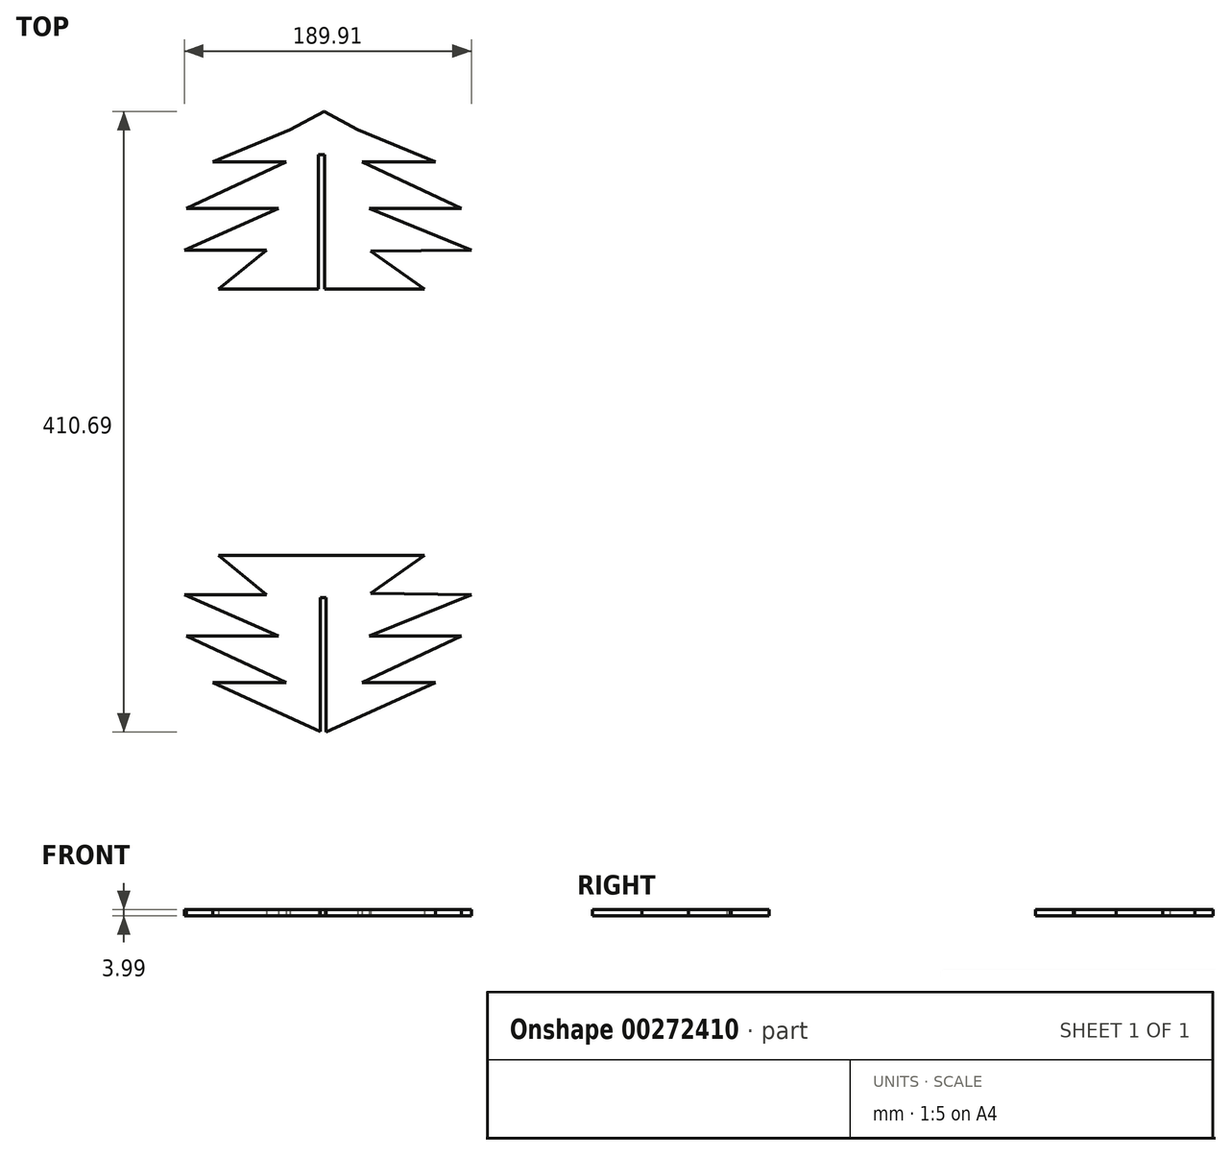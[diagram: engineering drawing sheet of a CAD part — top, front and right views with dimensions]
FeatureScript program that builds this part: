
annotation { "Feature Type Name" : "Feature", "Feature Type Description" : "" }
export const myFeature = defineFeature(function(context is Context, id is Id, definition is map)
    precondition{}
    {
        {
            var Q0;
            Q0=qCreatedBy(makeId("Top.planeOp"),FACE);
            var sketch = newSketch(context, id + "F0", { "sketchPlane" : qUnion([Q0])});
            skLineSegment(sketch, "E0.MirrorCS", {"start": v(-247.1, 88.4) * mm, "end": v(-298.41, 109.7) * mm});
            skLineSegment(sketch, "E1.MirrorCS", {"start": v(-295.66, 88.4) * mm, "end": v(-247.1, 88.4) * mm});
            skLineSegment(sketch, "E2.MirrorCS", {"start": v(-229.72, 57.49) * mm, "end": v(-295.66, 88.4) * mm});
            skLineSegment(sketch, "E3.MirrorCS", {"start": v(-290.86, 57.49) * mm, "end": v(-229.72, 57.49) * mm});
            skLineSegment(sketch, "E4.MirrorCS", {"start": v(-223.27, 30) * mm, "end": v(-290.86, 57.49) * mm});
            skLineSegment(sketch, "E5.MirrorCS", {"start": v(-289.8, 29.3) * mm, "end": v(-223.27, 30) * mm});
            skLineSegment(sketch, "E6.MirrorCS", {"start": v(-254.41, 4.11) * mm, "end": v(-289.8, 29.3) * mm});
            skLineSegment(sketch, "E7.MirrorCS", {"start": v(-320.45, 4.11) * mm, "end": v(-254.41, 4.11) * mm});
            skLineSegment(sketch, "E8.MirrorCS", {"start": v(-390.48, 4.11) * mm, "end": v(-324.44, 4.11) * mm});
            skLineSegment(sketch, "E9.MirrorCS", {"start": v(-390.48, 4.11) * mm, "end": v(-358.92, 30) * mm});
            skLineSegment(sketch, "E10.MirrorCS", {"start": v(-358.92, 30) * mm, "end": v(-413.18, 30) * mm});
            skLineSegment(sketch, "E11.MirrorCS", {"start": v(-350.67, 57.49) * mm, "end": v(-413.18, 30) * mm});
            skLineSegment(sketch, "E12.MirrorCS", {"start": v(-350.67, 57.49) * mm, "end": v(-411.8, 57.49) * mm});
            skLineSegment(sketch, "E13.MirrorCS", {"start": v(-411.8, 57.49) * mm, "end": v(-345.87, 88.4) * mm});
            skLineSegment(sketch, "E14.MirrorCS", {"start": v(-345.87, 88.4) * mm, "end": v(-394.42, 88.4) * mm});
            skLineSegment(sketch, "E15.MirrorCS", {"start": v(-394.42, 88.4) * mm, "end": v(-343.12, 109.7) * mm});
            skLineSegment(sketch, "E16.MirrorCS", {"start": v(-343.12, 109.7) * mm, "end": v(-320.76, 121.74) * mm});
            skLineSegment(sketch, "E17.MirrorCS", {"start": v(-298.41, 109.7) * mm, "end": v(-320.76, 121.74) * mm});
            skLineSegment(sketch, "E18", {"start": v(-324.44, 4.11) * mm, "end": v(-324.44, 93.01) * mm});
            skLineSegment(sketch, "E19", {"start": v(-324.44, 93.01) * mm, "end": v(-320.45, 93.01) * mm});
            skLineSegment(sketch, "E20", {"start": v(-320.45, 93.01) * mm, "end": v(-320.45, 4.11) * mm});
            skLineSegment(sketch, "E21", {"start": v(-546.98, -83.93) * mm, "end": v(-143.68, -83.93) * mm, "construction": true});
            skLineSegment(sketch, "E22.MirrorCS", {"start": v(-345.87, -256.27) * mm, "end": v(-394.42, -256.27) * mm});
            skLineSegment(sketch, "E23.MirrorCS", {"start": v(-411.8, -225.35) * mm, "end": v(-345.87, -256.27) * mm});
            skLineSegment(sketch, "E24.MirrorCS", {"start": v(-350.67, -225.35) * mm, "end": v(-411.8, -225.35) * mm});
            skLineSegment(sketch, "E25.MirrorCS", {"start": v(-350.67, -225.35) * mm, "end": v(-413.18, -197.88) * mm});
            skLineSegment(sketch, "E26.MirrorCS", {"start": v(-358.92, -197.88) * mm, "end": v(-413.18, -197.88) * mm});
            skLineSegment(sketch, "E27.MirrorCS", {"start": v(-390.48, -171.98) * mm, "end": v(-358.92, -197.88) * mm});
            skLineSegment(sketch, "E28.MirrorCS", {"start": v(-254.41, -171.98) * mm, "end": v(-289.8, -197.17) * mm});
            skLineSegment(sketch, "E29.MirrorCS", {"start": v(-289.8, -197.17) * mm, "end": v(-223.27, -197.88) * mm});
            skLineSegment(sketch, "E30.MirrorCS", {"start": v(-223.27, -197.88) * mm, "end": v(-290.86, -225.35) * mm});
            skLineSegment(sketch, "E31.MirrorCS", {"start": v(-290.86, -225.35) * mm, "end": v(-229.72, -225.35) * mm});
            skLineSegment(sketch, "E32.MirrorCS", {"start": v(-229.72, -225.35) * mm, "end": v(-295.66, -256.27) * mm});
            skLineSegment(sketch, "E33.MirrorCS", {"start": v(-295.66, -256.27) * mm, "end": v(-247.1, -256.27) * mm});
            skLineSegment(sketch, "E34", {"start": v(-390.48, -171.98) * mm, "end": v(-254.41, -171.98) * mm});
            skLineSegment(sketch, "E35", {"start": v(-319.3, -288.95) * mm, "end": v(-247.1, -256.27) * mm});
            skLineSegment(sketch, "E36", {"start": v(-394.42, -256.27) * mm, "end": v(-323.29, -288.47) * mm});
            skLineSegment(sketch, "E37", {"start": v(-323.29, -200.05) * mm, "end": v(-319.3, -200.05) * mm});
            skLineSegment(sketch, "E38", {"start": v(-323.29, -200.05) * mm, "end": v(-323.29, -288.47) * mm});
            skLineSegment(sketch, "E39", {"start": v(-319.3, -200.05) * mm, "end": v(-319.3, -288.95) * mm});
            skSolve(sketch);
        }
        {
            var Q0;
            Q0 = qSketchRegion(id + "F0", true);
            extrude(context, id + "F1", {"entities" : qUnion([Q0]), "depth" : 4 * mm});
        }
    });
